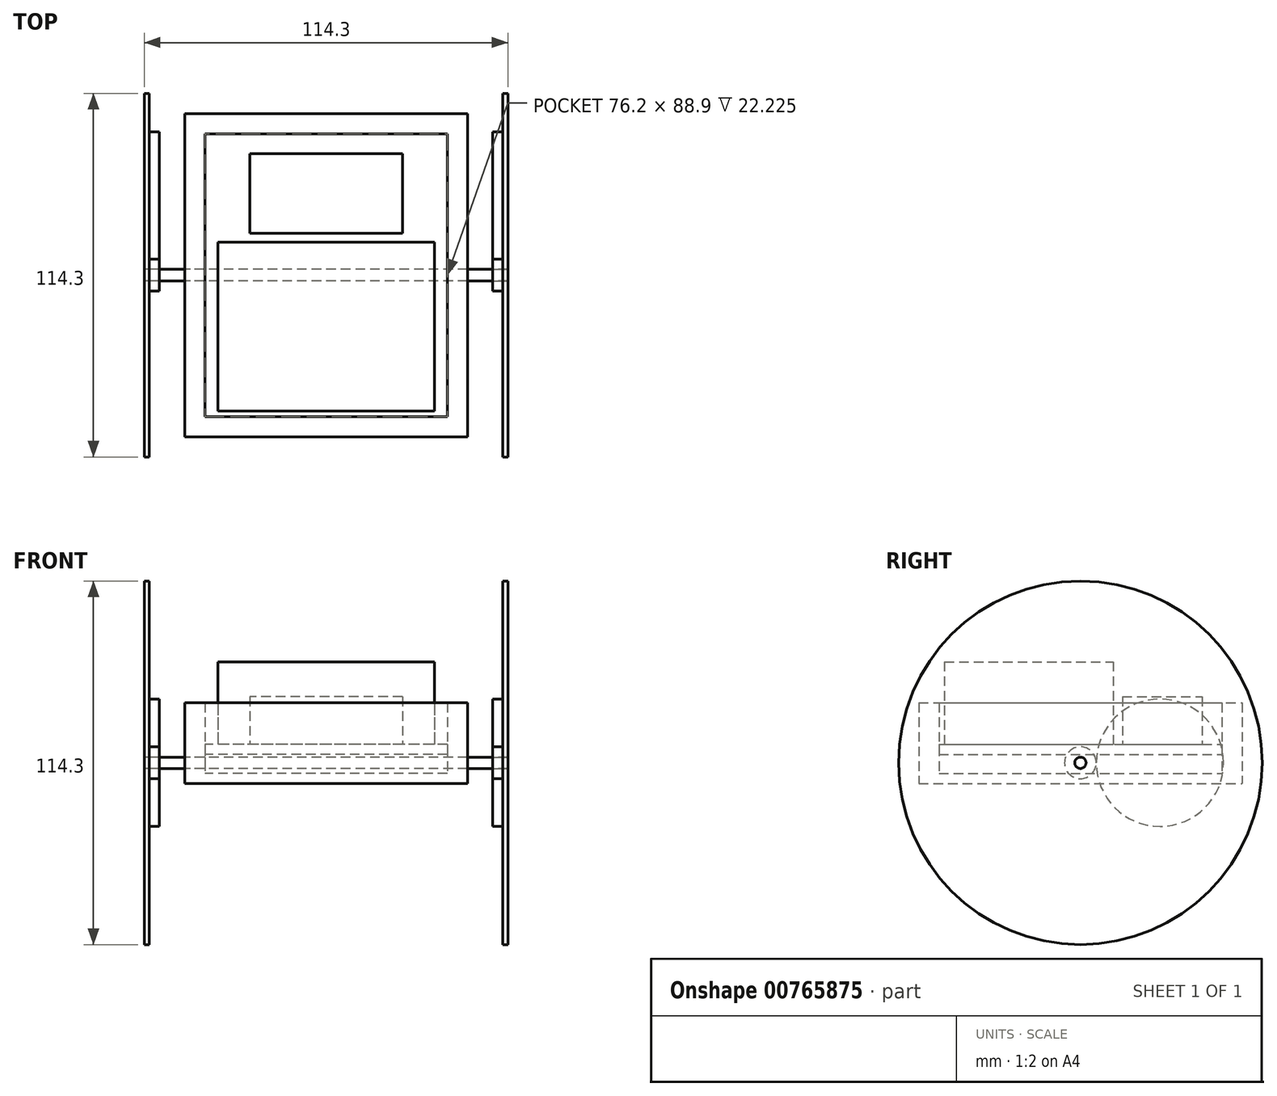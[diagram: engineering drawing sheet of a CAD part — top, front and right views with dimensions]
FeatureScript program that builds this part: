
annotation { "Feature Type Name" : "Feature", "Feature Type Description" : "" }
export const myFeature = defineFeature(function(context is Context, id is Id, definition is map)
    precondition{}
    {
        {
            var Q0;
            Q0=qCreatedBy(makeId("Top.planeOp"),FACE);
            var sketch = newSketch(context, id + "F0", { "sketchPlane" : qUnion([Q0])});
            skLineSegment(sketch, "E0.bottom", {"start": v(44.45, -50.8) * mm, "end": v(-44.45, -50.8) * mm});
            skLineSegment(sketch, "E0.top", {"start": v(44.45, 50.8) * mm, "end": v(-44.45, 50.8) * mm});
            skLineSegment(sketch, "E0.left", {"start": v(44.45, -50.8) * mm, "end": v(44.45, 50.8) * mm});
            skLineSegment(sketch, "E0.right", {"start": v(-44.45, -50.8) * mm, "end": v(-44.45, 50.8) * mm});
            skPoint(sketch, "E0.middle", {"position": v(0, 0) * mm});
            skLineSegment(sketch, "E1.bottom", {"start": v(38.1, -44.45) * mm, "end": v(-38.1, -44.45) * mm});
            skLineSegment(sketch, "E1.top", {"start": v(38.1, 44.45) * mm, "end": v(-38.1, 44.45) * mm});
            skLineSegment(sketch, "E1.left", {"start": v(38.1, -44.45) * mm, "end": v(38.1, 44.45) * mm});
            skLineSegment(sketch, "E1.right", {"start": v(-38.1, -44.45) * mm, "end": v(-38.1, 44.45) * mm});
            skSolve(sketch);
        }
        {
            var Q0;
            Q0=makeQuery(id+"F0.imprint","IMPRINT",FACE,{"disambiguationData":[TD([[makeQuery(id+"F0.imprint","IMPRINT",EDGE,{"derivedFrom":sQuery(id+"F0.wireOp",EDGE,"E0.bottom")}),-1.0]])]});
            extrude(context, id + "F1", {"entities" : qUnion([Q0]), "depth" : 25.4 * mm, "offsetDistance" : 25.4 * mm});
        }
        {
            var Q0;
            Q0=makeQuery(id+"F0.imprint","IMPRINT",FACE,{"disambiguationData":[TD([[makeQuery(id+"F0.imprint","IMPRINT",EDGE,{"derivedFrom":sQuery(id+"F0.wireOp",EDGE,"E1.bottom")}),-1.0]])]});
            extrude(context, id + "F2", {"entities" : qUnion([Q0]), "operationType" : NewBodyOperationType.ADD, "depth" : 3.17 * mm, "offsetDistance" : 25.4 * mm});
        }
        {
            var Q0;
            Q0=makeQuery(id+"F1.opExtrude","SWEPT_FACE",FACE,{"disambiguationData":[OSD([sQuery(id+"F0.wireOp",EDGE,"E1.right")])]});
            var sketch = newSketch(context, id + "F3", { "sketchPlane" : qUnion([Q0])});
            skLineSegment(sketch, "E2.bottom", {"start": v(-44.45, 12.3) * mm, "end": v(44.45, 12.3) * mm});
            skLineSegment(sketch, "E2.top", {"start": v(-44.45, 9.13) * mm, "end": v(44.45, 9.13) * mm});
            skLineSegment(sketch, "E2.left", {"start": v(-44.45, 12.3) * mm, "end": v(-44.45, 9.13) * mm});
            skLineSegment(sketch, "E2.right", {"start": v(44.45, 12.3) * mm, "end": v(44.45, 9.13) * mm});
            skSolve(sketch);
        }
        {
            var Q0;
            Q0=makeQuery(id+"F3.imprint","IMPRINT",FACE,{"disambiguationData":[TD([[makeQuery(id+"F3.imprint","IMPRINT",EDGE,{"derivedFrom":sQuery(id+"F3.wireOp",EDGE,"E2.bottom")}),-1.0]])]});
            extrude(context, id + "F4", {"entities" : qUnion([Q0]), "depth" : 76.2 * mm, "offsetDistance" : 25.4 * mm});
        }
        {
            var Q0;
            Q0=makeQuery(id+"F4.opExtrude","SWEPT_FACE",FACE,{"disambiguationData":[OSD([sQuery(id+"F3.wireOp",EDGE,"E2.bottom")])]});
            var sketch = newSketch(context, id + "F5", { "sketchPlane" : qUnion([Q0])});
            skLineSegment(sketch, "E3.bottom", {"start": v(24, 13.2) * mm, "end": v(-24, 13.2) * mm});
            skLineSegment(sketch, "E3.top", {"start": v(24, 38.2) * mm, "end": v(-24, 38.2) * mm});
            skLineSegment(sketch, "E3.left", {"start": v(24, 13.2) * mm, "end": v(24, 38.2) * mm});
            skLineSegment(sketch, "E3.right", {"start": v(-24, 13.2) * mm, "end": v(-24, 38.2) * mm});
            skPoint(sketch, "E3.middle", {"position": v(0, 25.7) * mm});
            skLineSegment(sketch, "E4.bottom", {"start": v(34, -42.7) * mm, "end": v(-34, -42.7) * mm});
            skLineSegment(sketch, "E4.top", {"start": v(34, 10.3) * mm, "end": v(-34, 10.3) * mm});
            skLineSegment(sketch, "E4.left", {"start": v(34, -42.7) * mm, "end": v(34, 10.3) * mm});
            skLineSegment(sketch, "E4.right", {"start": v(-34, -42.7) * mm, "end": v(-34, 10.3) * mm});
            skPoint(sketch, "E4.middle", {"position": v(0, -16.2) * mm});
            skSolve(sketch);
        }
        {
            var Q0;
            Q0=makeQuery(id+"F5.imprint","IMPRINT",FACE,{"disambiguationData":[TD([[makeQuery(id+"F5.imprint","IMPRINT",EDGE,{"derivedFrom":sQuery(id+"F5.wireOp",EDGE,"E3.bottom")}),-1.0]])]});
            extrude(context, id + "F6", {"entities" : qUnion([Q0]), "depth" : 15 * mm, "offsetDistance" : 25.4 * mm});
        }
        {
            var Q0;
            {var subQ0=sQuery(id+"F5.wireOp",EDGE,"E4.top");Q0=makeQuery(id+"F5.imprint","IMPRINT",FACE,{"disambiguationData":[TD([[makeQuery(id+"F5.imprint","IMPRINT",EDGE,{"derivedFrom":subQ0}),1.0]])]});}
            extrude(context, id + "F7", {"entities" : qUnion([Q0]), "depth" : 26 * mm, "offsetDistance" : 25.4 * mm});
        }
        {
            var Q0;
            Q0=makeQuery(id+"F1.opExtrude","SWEPT_FACE",FACE,{"disambiguationData":[OSD([sQuery(id+"F0.wireOp",EDGE,"E0.right")])]});
            var sketch = newSketch(context, id + "F8", { "sketchPlane" : qUnion([Q0])});
            skLineSegment(sketch, "E5", {"start": v(0, 0) * mm, "end": v(0, 25.4) * mm, "construction": true});
            skCircle(sketch, "E6", {"center": v(0, 6.55) * mm, "radius": 1.79 * mm});
            skSolve(sketch);
        }
        {
            var Q0;
            Q0=makeQuery(id+"F8.imprint","IMPRINT",FACE,{"disambiguationData":[TD([[makeQuery(id+"F8.imprint","IMPRINT",EDGE,{"derivedFrom":sQuery(id+"F8.wireOp",EDGE,"E6")}),1.0]])]});
            extrude(context, id + "F9", {"entities" : qUnion([Q0]), "operationType" : NewBodyOperationType.REMOVE, "oppositeDirection" : true, "depth" : 6.35 * mm, "offsetDistance" : 25.4 * mm});
        }
        {
            var Q0;
            Q0=makeQuery(id+"F1.opExtrude","SWEPT_FACE",FACE,{"disambiguationData":[OSD([sQuery(id+"F0.wireOp",EDGE,"E0.left")])]});
            var sketch = newSketch(context, id + "F10", { "sketchPlane" : qUnion([Q0])});
            skLineSegment(sketch, "E7", {"start": v(0, 0) * mm, "end": v(0, 25.4) * mm, "construction": true});
            skCircle(sketch, "E8", {"center": v(0, 6.55) * mm, "radius": 1.79 * mm});
            skSolve(sketch);
        }
        {
            var Q0;
            Q0=makeQuery(id+"F10.imprint","IMPRINT",FACE,{"disambiguationData":[TD([[makeQuery(id+"F10.imprint","IMPRINT",EDGE,{"derivedFrom":sQuery(id+"F10.wireOp",EDGE,"E8")}),1.0]])]});
            extrude(context, id + "F11", {"entities" : qUnion([Q0]), "operationType" : NewBodyOperationType.REMOVE, "oppositeDirection" : true, "depth" : 1 / 101.6 * mm, "offsetDistance" : 25.4 * mm});
        }
        {
            var Q0;
            Q0=makeQuery(id+"F8.imprint","IMPRINT",FACE,{"disambiguationData":[TD([[makeQuery(id+"F8.imprint","IMPRINT",EDGE,{"derivedFrom":sQuery(id+"F8.wireOp",EDGE,"E6")}),1.0]])]});
            extrude(context, id + "F12", {"entities" : qUnion([Q0]), "oppositeDirection" : true, "depth" : 57.15 * mm, "offsetDistance" : 25.4 * mm, "hasSecondDirection" : true, "secondDirectionOppositeDirection" : false, "secondDirectionDepth" : 57.15 * mm});
        }
        {
            var Q0;
            Q0=makeQuery(id+"F12.opExtrude","SWEPT_BODY",BODY,{"disambiguationData":[OSD([sQuery(id+"F8.wireOp",EDGE,"E6")])]});
            transform(context, id + "F13", {"entities" : qUnion([Q0]), "transformType" : TransformType.TRANSLATION_3D, "dx" : 38.1 * mm, "dy" : 0 * mm, "dz" : 0 * mm, "makeCopy" : false});
        }
        {
            var Q0;
            Q0=makeQuery(id+"F12.opExtrude","SWEPT_BODY",BODY,{"disambiguationData":[OSD([sQuery(id+"F8.wireOp",EDGE,"E6")])]});
            transform(context, id + "F14", {"entities" : qUnion([Q0]), "transformType" : TransformType.TRANSLATION_3D, "dx" : 6.35 * mm, "dy" : 0 * mm, "dz" : 0 * mm, "makeCopy" : false});
        }
        {
            var Q0;
            Q0=makeQuery(id+"F12.opExtrude","CAP_FACE",FACE,{"disambiguationData":[OSD([sQuery(id+"F8.wireOp",EDGE,"E6")])],"isStart":false});
            var sketch = newSketch(context, id + "F15", { "sketchPlane" : qUnion([Q0])});
            skCircle(sketch, "E9", {"center": v(0, 6.55) * mm, "radius": 57.15 * mm});
            skSolve(sketch);
        }
        {
            var Q0;
            Q0=makeQuery(id+"F15.imprint","IMPRINT",FACE,{"disambiguationData":[TD([[makeQuery(id+"F15.imprint","IMPRINT",EDGE,{"derivedFrom":sQuery(id+"F15.wireOp",EDGE,"E9")}),1.0]])]});
            extrude(context, id + "F16", {"entities" : qUnion([Q0]), "oppositeDirection" : true, "depth" : 1.59 * mm, "offsetDistance" : 25.4 * mm});
        }
        {
            var Q0;
            Q0=makeQuery(id+"F12.opExtrude","CAP_FACE",FACE,{"disambiguationData":[OSD([sQuery(id+"F8.wireOp",EDGE,"E6")])],"isStart":true});
            var sketch = newSketch(context, id + "F17", { "sketchPlane" : qUnion([Q0])});
            skCircle(sketch, "E10", {"center": v(0, 6.55) * mm, "radius": 57.15 * mm});
            skSolve(sketch);
        }
        {
            var Q0;
            Q0=makeQuery(id+"F17.imprint","IMPRINT",FACE,{"disambiguationData":[TD([[makeQuery(id+"F17.imprint","IMPRINT",EDGE,{"derivedFrom":sQuery(id+"F17.wireOp",EDGE,"E10")}),1.0]])]});
            extrude(context, id + "F18", {"entities" : qUnion([Q0]), "oppositeDirection" : true, "depth" : 1.59 * mm, "offsetDistance" : 25.4 * mm});
        }
        {
            var Q0;
            Q0=makeQuery(id+"F18.opExtrude","CAP_FACE",FACE,{"disambiguationData":[OSD([sQuery(id+"F8.wireOp",EDGE,"E6"),sQuery(id+"F17.wireOp",EDGE,"E10")])],"isStart":false});
            var sketch = newSketch(context, id + "F19", { "sketchPlane" : qUnion([Q0])});
            skSolve(sketch);
        }
        {
            var Q0;
            Q0=makeQuery(id+"F16.opExtrude","CAP_FACE",FACE,{"disambiguationData":[OSD([sQuery(id+"F8.wireOp",EDGE,"E6"),sQuery(id+"F15.wireOp",EDGE,"E9")])],"isStart":false});
            var sketch = newSketch(context, id + "F20", { "sketchPlane" : qUnion([Q0])});
            skCircle(sketch, "E11", {"center": v(0, 6.55) * mm, "radius": 5 * mm});
            skCircle(sketch, "E12", {"center": v(-25, 6.55) * mm, "radius": 20 * mm});
            skSolve(sketch);
        }
        {
            var Q0;
            Q0=makeQuery(id+"F20.imprint","IMPRINT",FACE,{"disambiguationData":[TD([[makeQuery(id+"F20.imprint","IMPRINT",EDGE,{"derivedFrom":sQuery(id+"F20.wireOp",EDGE,"E11")}),1.0]])]});
            extrude(context, id + "F21", {"entities" : qUnion([Q0]), "depth" : 3.17 * mm, "offsetDistance" : 25.4 * mm});
        }
        {
            var Q0;
            Q0=makeQuery(id+"F19.imprint","IMPRINT",FACE,{"disambiguationData":[TD([[makeQuery(id+"F19.imprint","IMPRINT",EDGE,{"derivedFrom":makeQuery(id+"F18.opExtrude","CAP_EDGE",EDGE,{"disambiguationData":[OSD([sQuery(id+"F17.wireOp",EDGE,"E10")])],"isStart":false})}),-1.0]])]});
            var sketch = newSketch(context, id + "F22", { "sketchPlane" : qUnion([Q0])});
            skCircle(sketch, "E13", {"center": v(0, 6.55) * mm, "radius": 5 * mm});
            skCircle(sketch, "E14", {"center": v(25, 6.55) * mm, "radius": 20 * mm});
            skSolve(sketch);
        }
        {
            var Q0;
            Q0=makeQuery(id+"F22.imprint","IMPRINT",FACE,{"disambiguationData":[TD([[makeQuery(id+"F22.imprint","IMPRINT",EDGE,{"derivedFrom":sQuery(id+"F22.wireOp",EDGE,"E13")}),1.0]])]});
            extrude(context, id + "F23", {"entities" : qUnion([Q0]), "depth" : 3.17 * mm, "offsetDistance" : 25.4 * mm});
        }
        {
            var Q0;
            Q0=makeQuery(id+"F20.imprint","IMPRINT",FACE,{"disambiguationData":[TD([[makeQuery(id+"F20.imprint","IMPRINT",EDGE,{"derivedFrom":sQuery(id+"F20.wireOp",EDGE,"E12")}),1.0]])]});
            extrude(context, id + "F24", {"entities" : qUnion([Q0]), "depth" : 3.17 * mm, "offsetDistance" : 25.4 * mm});
        }
        {
            var Q0;
            Q0=makeQuery(id+"F22.imprint","IMPRINT",FACE,{"disambiguationData":[TD([[makeQuery(id+"F22.imprint","IMPRINT",EDGE,{"derivedFrom":sQuery(id+"F22.wireOp",EDGE,"E14")}),1.0]])]});
            extrude(context, id + "F25", {"entities" : qUnion([Q0]), "depth" : 3.17 * mm, "offsetDistance" : 25.4 * mm});
        }
    });
